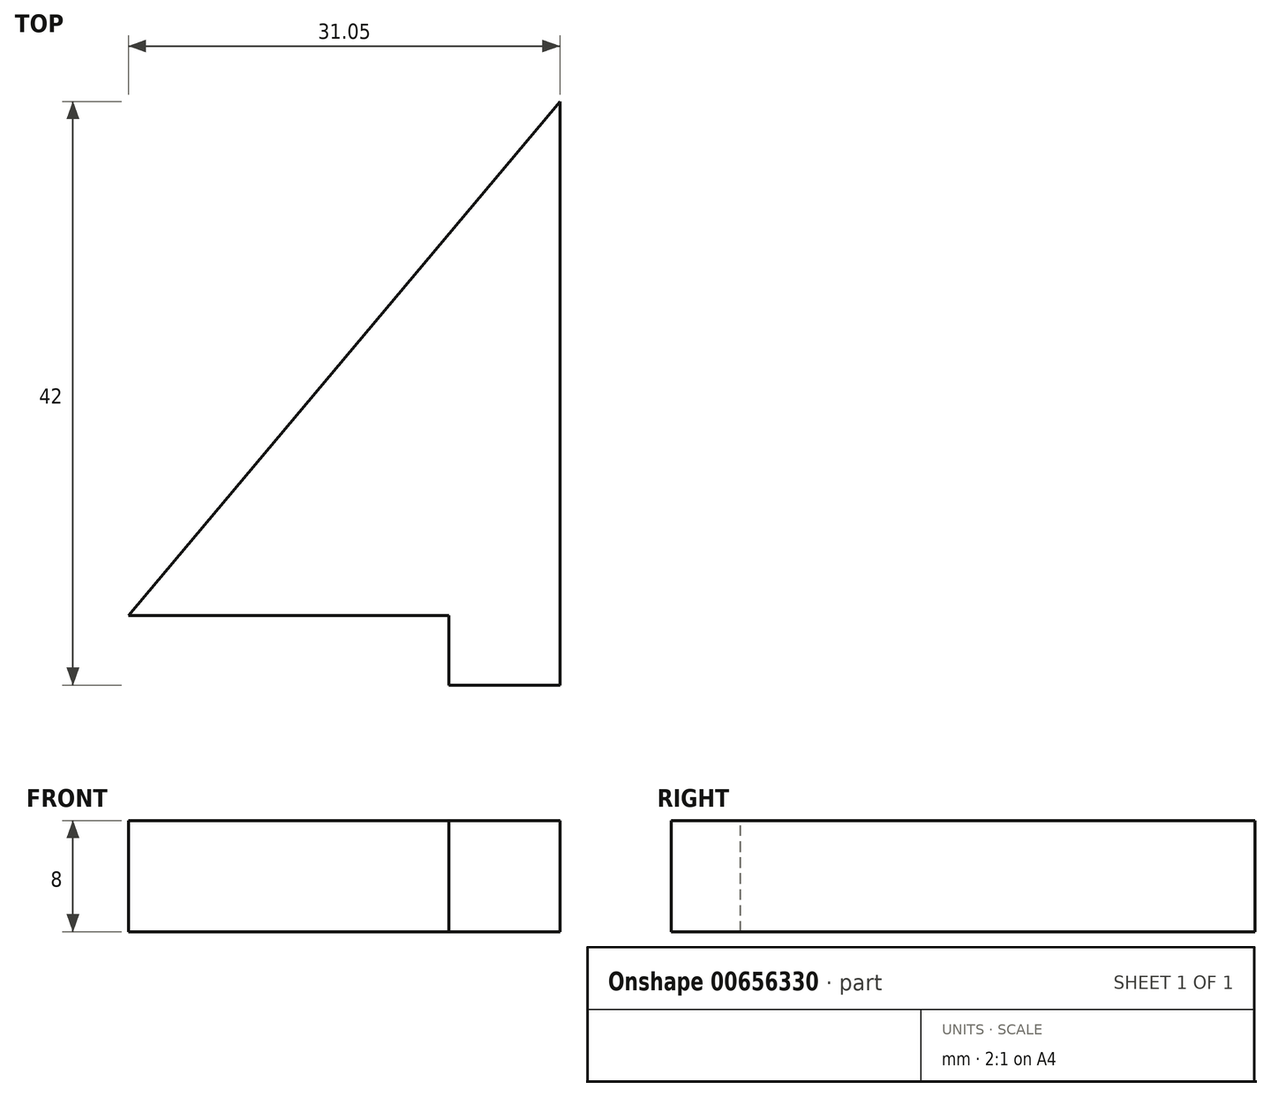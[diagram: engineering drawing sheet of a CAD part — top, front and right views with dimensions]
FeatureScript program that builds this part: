
annotation { "Feature Type Name" : "Feature", "Feature Type Description" : "" }
export const myFeature = defineFeature(function(context is Context, id is Id, definition is map)
    precondition{}
    {
        {
            var Q0;
            Q0=qCreatedBy(makeId("Top.planeOp"),FACE);
            var sketch = newSketch(context, id + "F0", { "sketchPlane" : qUnion([Q0])});
            skLineSegment(sketch, "E0", {"start": v(0, 0) * mm, "end": v(0, 37) * mm});
            skLineSegment(sketch, "E1", {"start": v(0, 37) * mm, "end": v(-31.05, 0) * mm});
            skLineSegment(sketch, "E2", {"start": v(-31.05, 0) * mm, "end": v(0, 0) * mm});
            skSolve(sketch);
        }
        {
            var Q0;
            Q0=makeQuery(id+"F0.imprint","IMPRINT",FACE,{"disambiguationData":[TD([[makeQuery(id+"F0.imprint","IMPRINT",EDGE,{"derivedFrom":sQuery(id+"F0.wireOp",EDGE,"E0")}),1.0]])]});
            extrude(context, id + "F1", {"entities" : qUnion([Q0]), "depth" : 8 * mm, "offsetDistance" : 25 * mm});
        }
        {
            var Q0;
            Q0=makeQuery(id+"F1.opExtrude","SWEPT_FACE",FACE,{"disambiguationData":[OSD([sQuery(id+"F0.wireOp",EDGE,"E2")])]});
            var sketch = newSketch(context, id + "F2", { "sketchPlane" : qUnion([Q0])});
            skLineSegment(sketch, "E3.bottom", {"start": v(0, 0) * mm, "end": v(-8, 0) * mm});
            skLineSegment(sketch, "E3.top", {"start": v(0, 8) * mm, "end": v(-8, 8) * mm});
            skLineSegment(sketch, "E3.left", {"start": v(0, 0) * mm, "end": v(0, 8) * mm});
            skLineSegment(sketch, "E3.right", {"start": v(-8, 0) * mm, "end": v(-8, 8) * mm});
            skSolve(sketch);
        }
        {
            var Q0;
            Q0=makeQuery(id+"F2.imprint","IMPRINT",FACE,{"disambiguationData":[TD([[makeQuery(id+"F2.imprint","IMPRINT",EDGE,{"derivedFrom":sQuery(id+"F2.wireOp",EDGE,"E3.bottom")}),1.0]])]});
            extrude(context, id + "F3", {"entities" : qUnion([Q0]), "operationType" : NewBodyOperationType.ADD, "depth" : 5 * mm, "offsetDistance" : 25 * mm});
        }
    });
